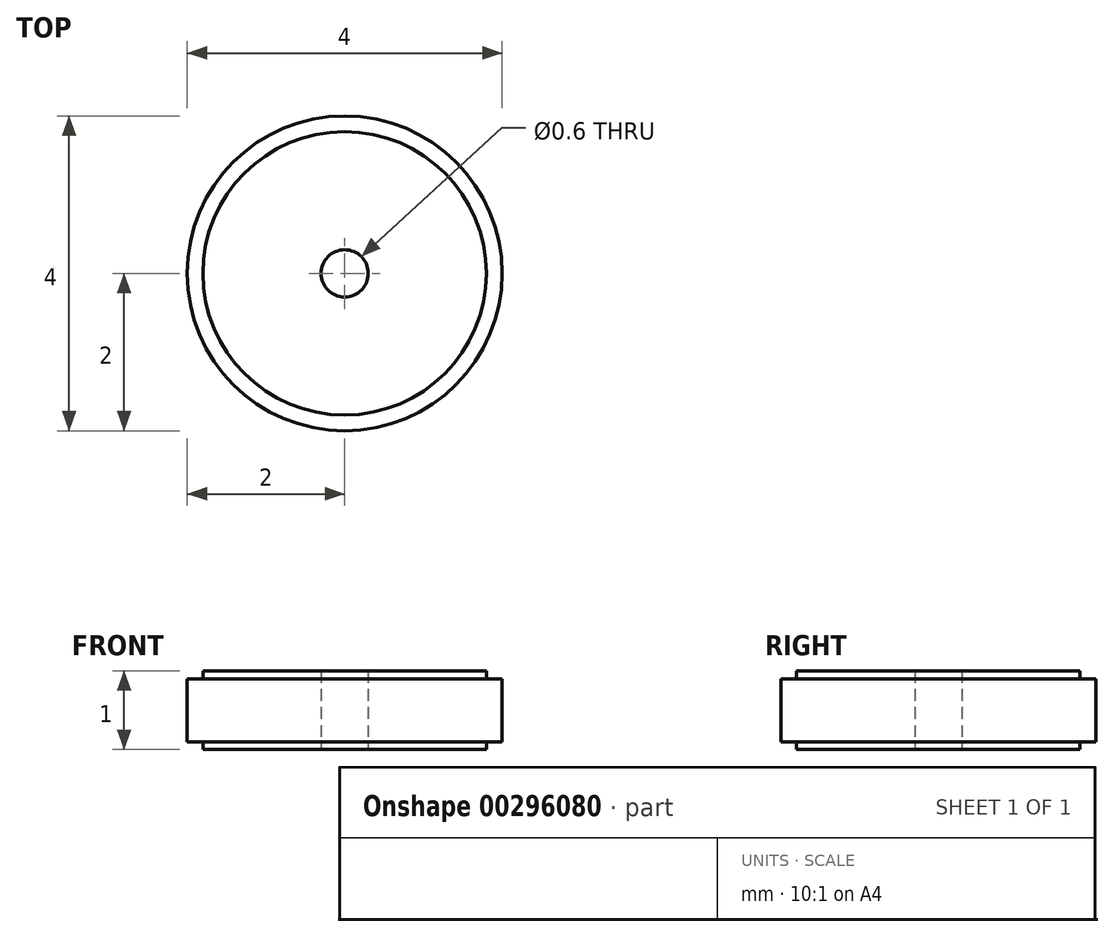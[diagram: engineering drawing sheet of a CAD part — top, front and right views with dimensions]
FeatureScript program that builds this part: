
annotation { "Feature Type Name" : "Feature", "Feature Type Description" : "" }
export const myFeature = defineFeature(function(context is Context, id is Id, definition is map)
    precondition{}
    {
        {
            var Q0;
            Q0=qCreatedBy(makeId("Top.planeOp"),FACE);
            var sketch = newSketch(context, id + "F0", { "sketchPlane" : qUnion([Q0])});
            skCircle(sketch, "E0", {"center": v(0, 0) * mm, "radius": 2 * mm});
            skCircle(sketch, "E1", {"center": v(0, 0) * mm, "radius": 0.3 * mm});
            skSolve(sketch);
        }
        {
            var Q0;
            Q0=qSketchRegion(id+"F0",true);
            extrude(context, id + "F1", {"entities" : qUnion([Q0]), "depth" : 1 * mm});
        }
        {
            var Q0;
            Q0=makeQuery(id+"F1.opExtrude","CAP_FACE",FACE,{"disambiguationData":[OSD([sQuery(id+"F0.wireOp",EDGE,"E0"),sQuery(id+"F0.wireOp",EDGE,"E1")])],"isStart":false});
            var sketch = newSketch(context, id + "F2", { "sketchPlane" : qUnion([Q0])});
            skCircle(sketch, "E2", {"center": v(0, 0) * mm, "radius": 1.8 * mm});
            skCircle(sketch, "E3", {"center": v(0, 0) * mm, "radius": 2.01 * mm});
            skSolve(sketch);
        }
        {
            var Q0;
            Q0 = qSketchRegion(id + "F2", true);
            extrude(context, id + "F3", {"entities" : qUnion([Q0]), "operationType" : NewBodyOperationType.REMOVE, "oppositeDirection" : true, "depth" : 0.1 * mm});
        }
        {
            var Q0;
            Q0=makeQuery(id+"F0.imprint","IMPRINT",FACE,{"disambiguationData":[TD([[makeQuery(id+"F0.imprint","IMPRINT",EDGE,{"derivedFrom":sQuery(id+"F0.wireOp",EDGE,"E0")}),1.0]])]});
            var sketch = newSketch(context, id + "F4", { "sketchPlane" : qUnion([Q0])});
            skCircle(sketch, "E4", {"center": v(0, 0) * mm, "radius": 1.8 * mm});
            skCircle(sketch, "E5", {"center": v(0, 0) * mm, "radius": 2 * mm});
            skSolve(sketch);
        }
        {
            var Q0;
            Q0 = qSketchRegion(id + "F4", true);
            extrude(context, id + "F5", {"entities" : qUnion([Q0]), "operationType" : NewBodyOperationType.REMOVE, "depth" : 0.1 * mm});
        }
    });
